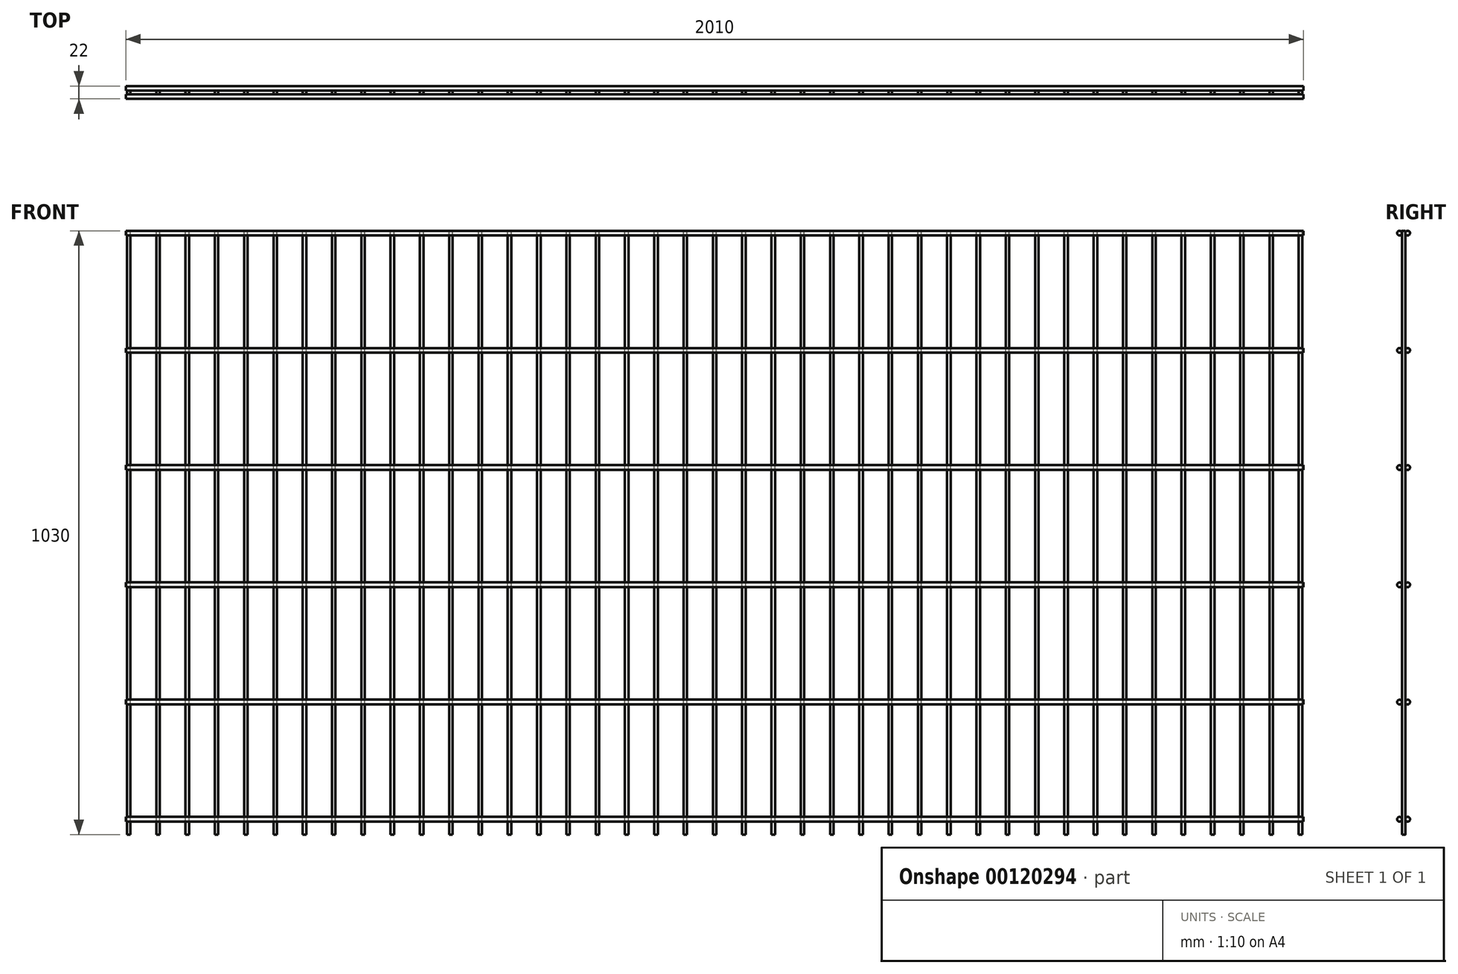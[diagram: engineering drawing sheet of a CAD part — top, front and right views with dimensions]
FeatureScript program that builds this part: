
annotation { "Feature Type Name" : "Feature", "Feature Type Description" : "" }
export const myFeature = defineFeature(function(context is Context, id is Id, definition is map)
    precondition{}
    {
        {
            var Q0;
            Q0=qCreatedBy(makeId("Top.planeOp"),FACE);
            var sketch = newSketch(context, id + "F0", { "sketchPlane" : qUnion([Q0])});
            skCircle(sketch, "E0", {"center": v(-100, 0) * mm, "radius": 3 * mm});
            skCircle(sketch, "E1", {"center": v(-150, 0) * mm, "radius": 3 * mm});
            skCircle(sketch, "E2", {"center": v(-50, 0) * mm, "radius": 3 * mm});
            skCircle(sketch, "E3", {"center": v(0, 0) * mm, "radius": 3 * mm});
            skCircle(sketch, "E4", {"center": v(100, 0) * mm, "radius": 3 * mm});
            skCircle(sketch, "E5", {"center": v(50, 0) * mm, "radius": 3 * mm});
            skCircle(sketch, "E6", {"center": v(150, 0) * mm, "radius": 3 * mm});
            skCircle(sketch, "E7", {"center": v(-450, 0) * mm, "radius": 3 * mm});
            skCircle(sketch, "E8", {"center": v(-500, 0) * mm, "radius": 3 * mm});
            skCircle(sketch, "E9", {"center": v(-400, 0) * mm, "radius": 3 * mm});
            skCircle(sketch, "E10", {"center": v(-350, 0) * mm, "radius": 3 * mm});
            skCircle(sketch, "E11", {"center": v(-250, 0) * mm, "radius": 3 * mm});
            skCircle(sketch, "E12", {"center": v(-300, 0) * mm, "radius": 3 * mm});
            skCircle(sketch, "E13", {"center": v(-200, 0) * mm, "radius": 3 * mm});
            skCircle(sketch, "E14", {"center": v(250, 0) * mm, "radius": 3 * mm});
            skCircle(sketch, "E15", {"center": v(200, 0) * mm, "radius": 3 * mm});
            skCircle(sketch, "E16", {"center": v(300, 0) * mm, "radius": 3 * mm});
            skCircle(sketch, "E17", {"center": v(350, 0) * mm, "radius": 3 * mm});
            skCircle(sketch, "E18", {"center": v(450, 0) * mm, "radius": 3 * mm});
            skCircle(sketch, "E19", {"center": v(400, 0) * mm, "radius": 3 * mm});
            skCircle(sketch, "E20", {"center": v(500, 0) * mm, "radius": 3 * mm});
            skCircle(sketch, "E21", {"center": v(600, 0) * mm, "radius": 3 * mm});
            skCircle(sketch, "E22", {"center": v(550, 0) * mm, "radius": 3 * mm});
            skCircle(sketch, "E23", {"center": v(650, 0) * mm, "radius": 3 * mm});
            skCircle(sketch, "E24", {"center": v(750, 0) * mm, "radius": 3 * mm});
            skCircle(sketch, "E25", {"center": v(700, 0) * mm, "radius": 3 * mm});
            skCircle(sketch, "E26", {"center": v(800, 0) * mm, "radius": 3 * mm});
            skCircle(sketch, "E27", {"center": v(850, 0) * mm, "radius": 3 * mm});
            skCircle(sketch, "E28", {"center": v(950, 0) * mm, "radius": 3 * mm});
            skCircle(sketch, "E29", {"center": v(900, 0) * mm, "radius": 3 * mm});
            skCircle(sketch, "E30", {"center": v(1000, 0) * mm, "radius": 3 * mm});
            skCircle(sketch, "E31", {"center": v(-950, 0) * mm, "radius": 3 * mm});
            skCircle(sketch, "E32", {"center": v(-1000, 0) * mm, "radius": 3 * mm});
            skCircle(sketch, "E33", {"center": v(-900, 0) * mm, "radius": 3 * mm});
            skCircle(sketch, "E34", {"center": v(-800, 0) * mm, "radius": 3 * mm});
            skCircle(sketch, "E35", {"center": v(-850, 0) * mm, "radius": 3 * mm});
            skCircle(sketch, "E36", {"center": v(-750, 0) * mm, "radius": 3 * mm});
            skCircle(sketch, "E37", {"center": v(-700, 0) * mm, "radius": 3 * mm});
            skCircle(sketch, "E38", {"center": v(-600, 0) * mm, "radius": 3 * mm});
            skCircle(sketch, "E39", {"center": v(-650, 0) * mm, "radius": 3 * mm});
            skCircle(sketch, "E40", {"center": v(-550, 0) * mm, "radius": 3 * mm});
            skSolve(sketch);
        }
        {
            var Q0;
            Q0=makeQuery(id+"F0.imprint","IMPRINT",FACE,{"disambiguationData":[TD([[makeQuery(id+"F0.imprint","IMPRINT",EDGE,{"derivedFrom":sQuery(id+"F0.wireOp",EDGE,"E24")}),1.0]])]});
            var Q1;
            Q1=makeQuery(id+"F0.imprint","IMPRINT",FACE,{"disambiguationData":[TD([[makeQuery(id+"F0.imprint","IMPRINT",EDGE,{"derivedFrom":sQuery(id+"F0.wireOp",EDGE,"E40")}),1.0]])]});
            var Q2;
            Q2=makeQuery(id+"F0.imprint","IMPRINT",FACE,{"disambiguationData":[TD([[makeQuery(id+"F0.imprint","IMPRINT",EDGE,{"derivedFrom":sQuery(id+"F0.wireOp",EDGE,"E28")}),1.0]])]});
            var Q3;
            Q3=makeQuery(id+"F0.imprint","IMPRINT",FACE,{"disambiguationData":[TD([[makeQuery(id+"F0.imprint","IMPRINT",EDGE,{"derivedFrom":sQuery(id+"F0.wireOp",EDGE,"E18")}),1.0]])]});
            var Q4;
            Q4=makeQuery(id+"F0.imprint","IMPRINT",FACE,{"disambiguationData":[TD([[makeQuery(id+"F0.imprint","IMPRINT",EDGE,{"derivedFrom":sQuery(id+"F0.wireOp",EDGE,"E34")}),1.0]])]});
            var Q5;
            Q5=makeQuery(id+"F0.imprint","IMPRINT",FACE,{"disambiguationData":[TD([[makeQuery(id+"F0.imprint","IMPRINT",EDGE,{"derivedFrom":sQuery(id+"F0.wireOp",EDGE,"E33")}),1.0]])]});
            var Q6;
            Q6=makeQuery(id+"F0.imprint","IMPRINT",FACE,{"disambiguationData":[TD([[makeQuery(id+"F0.imprint","IMPRINT",EDGE,{"derivedFrom":sQuery(id+"F0.wireOp",EDGE,"E17")}),1.0]])]});
            var Q7;
            Q7=makeQuery(id+"F0.imprint","IMPRINT",FACE,{"disambiguationData":[TD([[makeQuery(id+"F0.imprint","IMPRINT",EDGE,{"derivedFrom":sQuery(id+"F0.wireOp",EDGE,"E37")}),1.0]])]});
            var Q8;
            Q8=makeQuery(id+"F0.imprint","IMPRINT",FACE,{"disambiguationData":[TD([[makeQuery(id+"F0.imprint","IMPRINT",EDGE,{"derivedFrom":sQuery(id+"F0.wireOp",EDGE,"E30")}),1.0]])]});
            var Q9;
            Q9=makeQuery(id+"F0.imprint","IMPRINT",FACE,{"disambiguationData":[TD([[makeQuery(id+"F0.imprint","IMPRINT",EDGE,{"derivedFrom":sQuery(id+"F0.wireOp",EDGE,"E21")}),1.0]])]});
            var Q10;
            Q10=makeQuery(id+"F0.imprint","IMPRINT",FACE,{"disambiguationData":[TD([[makeQuery(id+"F0.imprint","IMPRINT",EDGE,{"derivedFrom":sQuery(id+"F0.wireOp",EDGE,"E25")}),1.0]])]});
            var Q11;
            Q11=makeQuery(id+"F0.imprint","IMPRINT",FACE,{"disambiguationData":[TD([[makeQuery(id+"F0.imprint","IMPRINT",EDGE,{"derivedFrom":sQuery(id+"F0.wireOp",EDGE,"E23")}),1.0]])]});
            var Q12;
            Q12=makeQuery(id+"F0.imprint","IMPRINT",FACE,{"disambiguationData":[TD([[makeQuery(id+"F0.imprint","IMPRINT",EDGE,{"derivedFrom":sQuery(id+"F0.wireOp",EDGE,"E39")}),1.0]])]});
            var Q13;
            Q13=makeQuery(id+"F0.imprint","IMPRINT",FACE,{"disambiguationData":[TD([[makeQuery(id+"F0.imprint","IMPRINT",EDGE,{"derivedFrom":sQuery(id+"F0.wireOp",EDGE,"E27")}),1.0]])]});
            var Q14;
            Q14=makeQuery(id+"F0.imprint","IMPRINT",FACE,{"disambiguationData":[TD([[makeQuery(id+"F0.imprint","IMPRINT",EDGE,{"derivedFrom":sQuery(id+"F0.wireOp",EDGE,"E12")}),1.0]])]});
            var Q15;
            Q15=makeQuery(id+"F0.imprint","IMPRINT",FACE,{"disambiguationData":[TD([[makeQuery(id+"F0.imprint","IMPRINT",EDGE,{"derivedFrom":sQuery(id+"F0.wireOp",EDGE,"E11")}),1.0]])]});
            var Q16;
            Q16=makeQuery(id+"F0.imprint","IMPRINT",FACE,{"disambiguationData":[TD([[makeQuery(id+"F0.imprint","IMPRINT",EDGE,{"derivedFrom":sQuery(id+"F0.wireOp",EDGE,"E10")}),1.0]])]});
            var Q17;
            Q17=makeQuery(id+"F0.imprint","IMPRINT",FACE,{"disambiguationData":[TD([[makeQuery(id+"F0.imprint","IMPRINT",EDGE,{"derivedFrom":sQuery(id+"F0.wireOp",EDGE,"E9")}),1.0]])]});
            var Q18;
            Q18=makeQuery(id+"F0.imprint","IMPRINT",FACE,{"disambiguationData":[TD([[makeQuery(id+"F0.imprint","IMPRINT",EDGE,{"derivedFrom":sQuery(id+"F0.wireOp",EDGE,"E8")}),1.0]])]});
            var Q19;
            Q19=makeQuery(id+"F0.imprint","IMPRINT",FACE,{"disambiguationData":[TD([[makeQuery(id+"F0.imprint","IMPRINT",EDGE,{"derivedFrom":sQuery(id+"F0.wireOp",EDGE,"E31")}),1.0]])]});
            var Q20;
            Q20=makeQuery(id+"F0.imprint","IMPRINT",FACE,{"disambiguationData":[TD([[makeQuery(id+"F0.imprint","IMPRINT",EDGE,{"derivedFrom":sQuery(id+"F0.wireOp",EDGE,"E7")}),1.0]])]});
            var Q21;
            Q21=makeQuery(id+"F0.imprint","IMPRINT",FACE,{"disambiguationData":[TD([[makeQuery(id+"F0.imprint","IMPRINT",EDGE,{"derivedFrom":sQuery(id+"F0.wireOp",EDGE,"E6")}),1.0]])]});
            var Q22;
            Q22=makeQuery(id+"F0.imprint","IMPRINT",FACE,{"disambiguationData":[TD([[makeQuery(id+"F0.imprint","IMPRINT",EDGE,{"derivedFrom":sQuery(id+"F0.wireOp",EDGE,"E5")}),1.0]])]});
            var Q23;
            Q23=makeQuery(id+"F0.imprint","IMPRINT",FACE,{"disambiguationData":[TD([[makeQuery(id+"F0.imprint","IMPRINT",EDGE,{"derivedFrom":sQuery(id+"F0.wireOp",EDGE,"E4")}),1.0]])]});
            var Q24;
            Q24=makeQuery(id+"F0.imprint","IMPRINT",FACE,{"disambiguationData":[TD([[makeQuery(id+"F0.imprint","IMPRINT",EDGE,{"derivedFrom":sQuery(id+"F0.wireOp",EDGE,"E3")}),1.0]])]});
            var Q25;
            Q25=makeQuery(id+"F0.imprint","IMPRINT",FACE,{"disambiguationData":[TD([[makeQuery(id+"F0.imprint","IMPRINT",EDGE,{"derivedFrom":sQuery(id+"F0.wireOp",EDGE,"E2")}),1.0]])]});
            var Q26;
            Q26=makeQuery(id+"F0.imprint","IMPRINT",FACE,{"disambiguationData":[TD([[makeQuery(id+"F0.imprint","IMPRINT",EDGE,{"derivedFrom":sQuery(id+"F0.wireOp",EDGE,"E1")}),1.0]])]});
            var Q27;
            Q27=makeQuery(id+"F0.imprint","IMPRINT",FACE,{"disambiguationData":[TD([[makeQuery(id+"F0.imprint","IMPRINT",EDGE,{"derivedFrom":sQuery(id+"F0.wireOp",EDGE,"E0")}),1.0]])]});
            var Q28;
            Q28=makeQuery(id+"F0.imprint","IMPRINT",FACE,{"disambiguationData":[TD([[makeQuery(id+"F0.imprint","IMPRINT",EDGE,{"derivedFrom":sQuery(id+"F0.wireOp",EDGE,"E32")}),1.0]])]});
            var Q29;
            Q29=makeQuery(id+"F0.imprint","IMPRINT",FACE,{"disambiguationData":[TD([[makeQuery(id+"F0.imprint","IMPRINT",EDGE,{"derivedFrom":sQuery(id+"F0.wireOp",EDGE,"E16")}),1.0]])]});
            var Q30;
            Q30=makeQuery(id+"F0.imprint","IMPRINT",FACE,{"disambiguationData":[TD([[makeQuery(id+"F0.imprint","IMPRINT",EDGE,{"derivedFrom":sQuery(id+"F0.wireOp",EDGE,"E14")}),1.0]])]});
            var Q31;
            Q31=makeQuery(id+"F0.imprint","IMPRINT",FACE,{"disambiguationData":[TD([[makeQuery(id+"F0.imprint","IMPRINT",EDGE,{"derivedFrom":sQuery(id+"F0.wireOp",EDGE,"E13")}),1.0]])]});
            var Q32;
            Q32=makeQuery(id+"F0.imprint","IMPRINT",FACE,{"disambiguationData":[TD([[makeQuery(id+"F0.imprint","IMPRINT",EDGE,{"derivedFrom":sQuery(id+"F0.wireOp",EDGE,"E29")}),1.0]])]});
            var Q33;
            Q33=makeQuery(id+"F0.imprint","IMPRINT",FACE,{"disambiguationData":[TD([[makeQuery(id+"F0.imprint","IMPRINT",EDGE,{"derivedFrom":sQuery(id+"F0.wireOp",EDGE,"E36")}),1.0]])]});
            var Q34;
            Q34=makeQuery(id+"F0.imprint","IMPRINT",FACE,{"disambiguationData":[TD([[makeQuery(id+"F0.imprint","IMPRINT",EDGE,{"derivedFrom":sQuery(id+"F0.wireOp",EDGE,"E15")}),1.0]])]});
            var Q35;
            Q35=makeQuery(id+"F0.imprint","IMPRINT",FACE,{"disambiguationData":[TD([[makeQuery(id+"F0.imprint","IMPRINT",EDGE,{"derivedFrom":sQuery(id+"F0.wireOp",EDGE,"E20")}),1.0]])]});
            var Q36;
            Q36=makeQuery(id+"F0.imprint","IMPRINT",FACE,{"disambiguationData":[TD([[makeQuery(id+"F0.imprint","IMPRINT",EDGE,{"derivedFrom":sQuery(id+"F0.wireOp",EDGE,"E22")}),1.0]])]});
            var Q37;
            Q37=makeQuery(id+"F0.imprint","IMPRINT",FACE,{"disambiguationData":[TD([[makeQuery(id+"F0.imprint","IMPRINT",EDGE,{"derivedFrom":sQuery(id+"F0.wireOp",EDGE,"E38")}),1.0]])]});
            var Q38;
            Q38=makeQuery(id+"F0.imprint","IMPRINT",FACE,{"disambiguationData":[TD([[makeQuery(id+"F0.imprint","IMPRINT",EDGE,{"derivedFrom":sQuery(id+"F0.wireOp",EDGE,"E26")}),1.0]])]});
            var Q39;
            Q39=makeQuery(id+"F0.imprint","IMPRINT",FACE,{"disambiguationData":[TD([[makeQuery(id+"F0.imprint","IMPRINT",EDGE,{"derivedFrom":sQuery(id+"F0.wireOp",EDGE,"E35")}),1.0]])]});
            var Q40;
            Q40=makeQuery(id+"F0.imprint","IMPRINT",FACE,{"disambiguationData":[TD([[makeQuery(id+"F0.imprint","IMPRINT",EDGE,{"derivedFrom":sQuery(id+"F0.wireOp",EDGE,"E19")}),1.0]])]});
            extrude(context, id + "F1", {"entities" : qUnion([Q0, Q1, Q2, Q3, Q4, Q5, Q6, Q7, Q8, Q9, Q10, Q11, Q12, Q13, Q14, Q15, Q16, Q17, Q18, Q19, Q20, Q21, Q22, Q23, Q24, Q25, Q26, Q27, Q28, Q29, Q30, Q31, Q32, Q33, Q34, Q35, Q36, Q37, Q38, Q39, Q40]), "oppositeDirection" : true, "depth" : 1030 * mm});
        }
        {
            var Q0;
            Q0=qCreatedBy(makeId("Right.planeOp"),FACE);
            var sketch = newSketch(context, id + "F2", { "sketchPlane" : qUnion([Q0])});
            skLineSegment(sketch, "E41", {"start": v(-7, 0) * mm, "end": v(-7, -1029.94) * mm, "construction": true});
            skLineSegment(sketch, "E42", {"start": v(7, 0) * mm, "end": v(7, -1029.46) * mm, "construction": true});
            skCircle(sketch, "E43", {"center": v(7, -4) * mm, "radius": 4 * mm});
            skCircle(sketch, "E44", {"center": v(-7, -4) * mm, "radius": 4 * mm});
            skCircle(sketch, "E45", {"center": v(7, -204) * mm, "radius": 4 * mm});
            skCircle(sketch, "E46", {"center": v(-7, -204) * mm, "radius": 4 * mm});
            skCircle(sketch, "E47", {"center": v(7, -404) * mm, "radius": 4 * mm});
            skCircle(sketch, "E48", {"center": v(-7, -404) * mm, "radius": 4 * mm});
            skCircle(sketch, "E49", {"center": v(7, -604) * mm, "radius": 4 * mm});
            skCircle(sketch, "E50", {"center": v(-7, -604) * mm, "radius": 4 * mm});
            skCircle(sketch, "E51", {"center": v(7, -804) * mm, "radius": 4 * mm});
            skCircle(sketch, "E52", {"center": v(-7, -804) * mm, "radius": 4 * mm});
            skCircle(sketch, "E53", {"center": v(7, -1004) * mm, "radius": 4 * mm});
            skCircle(sketch, "E54", {"center": v(-7, -1004) * mm, "radius": 4 * mm});
            skSolve(sketch);
        }
        {
            var Q0;
            Q0=qSketchRegion(id+"F2",true);
            extrude(context, id + "F3", {"entities" : qUnion([Q0]), "depth" : 2010 * mm, "symmetric" : true});
        }
    });
